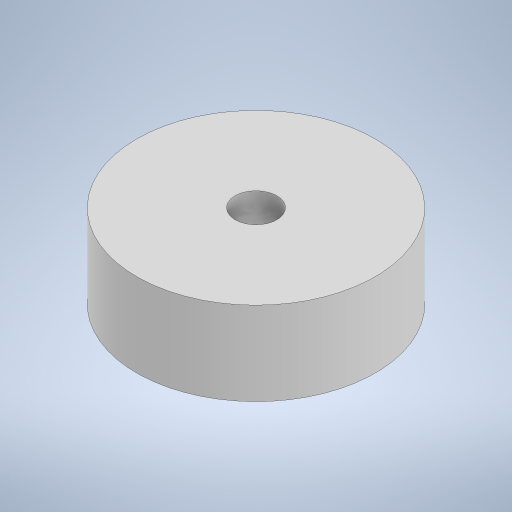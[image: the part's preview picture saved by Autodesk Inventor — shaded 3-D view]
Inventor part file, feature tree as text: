
AUTODESK INVENTOR PART (.ipt)
format: ipt  version: 2024.1 (Build 281209000, 209)  size: 199,680 bytes
history: native  units: mm
features: other x1, extrude x1, sketch x1
ambient origin geometry x8: Origin, YZ Plane, XZ Plane, XY Plane, X Axis, Y Axis, Z Axis, Center Point
bodies: Body1 (feature_tree)
feature tree (3):
  other  "ソリッド1"
  extrude  "押し出し1"  Depth=20.0mm
  sketch  "スケッチ1"
